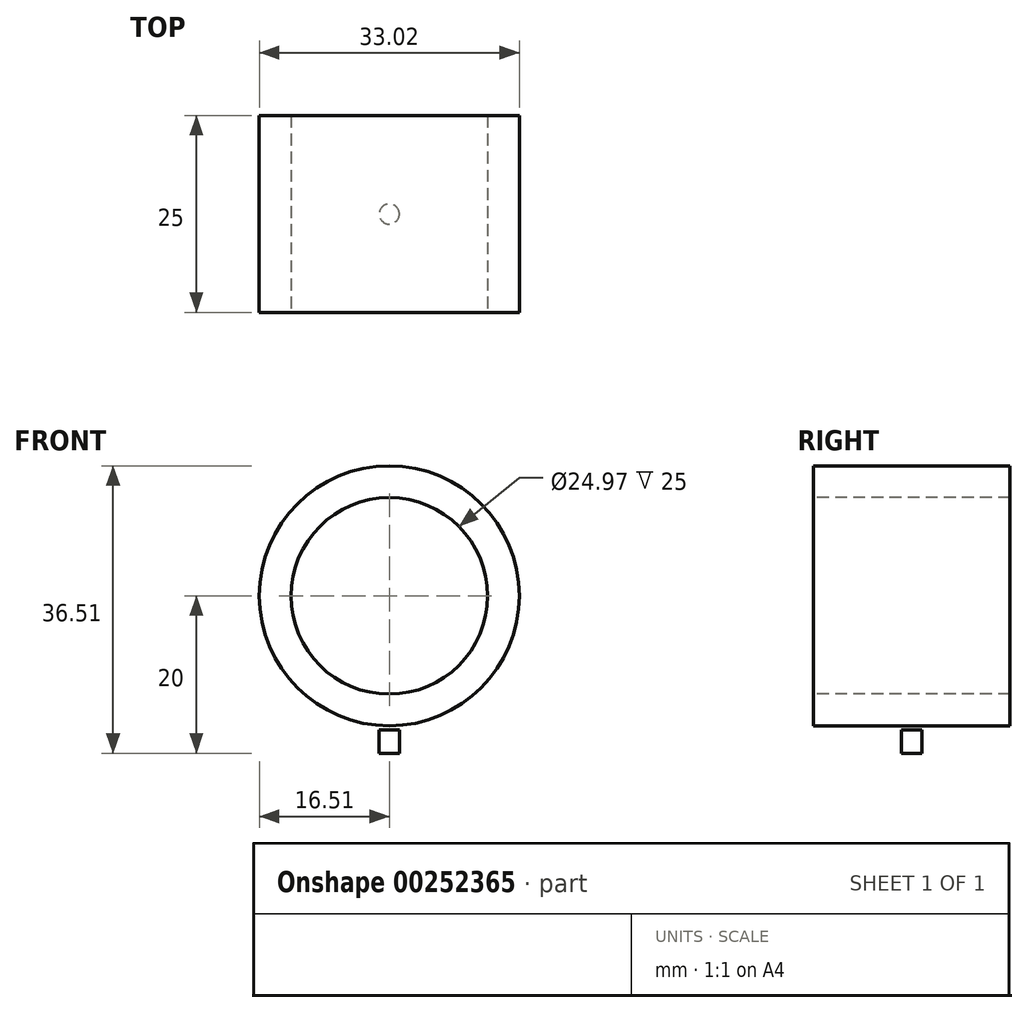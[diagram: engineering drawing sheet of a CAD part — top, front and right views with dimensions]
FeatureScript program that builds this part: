
annotation { "Feature Type Name" : "Feature", "Feature Type Description" : "" }
export const myFeature = defineFeature(function(context is Context, id is Id, definition is map)
    precondition{}
    {
        {
            var Q0;
            Q0=qCreatedBy(makeId("Front.planeOp"),FACE);
            var sketch = newSketch(context, id + "F0", { "sketchPlane" : qUnion([Q0])});
            skCircle(sketch, "E0", {"center": v(0, 0) * mm, "radius": 16.51 * mm});
            skLineSegment(sketch, "E1.bottom", {"start": v(3.39, -18.5) * mm, "end": v(-3.39, -18.5) * mm});
            skLineSegment(sketch, "E1.top", {"start": v(3.39, -14.53) * mm, "end": v(-3.39, -14.53) * mm});
            skLineSegment(sketch, "E1.left", {"start": v(3.39, -18.5) * mm, "end": v(3.39, -14.53) * mm});
            skLineSegment(sketch, "E1.right", {"start": v(-3.39, -18.5) * mm, "end": v(-3.39, -14.53) * mm});
            skPoint(sketch, "E1.middle", {"position": v(0, -16.51) * mm});
            skSolve(sketch);
        }
        {
            var Q0;
            Q0=makeQuery(id+"F0.imprint","IMPRINT",FACE,{"disambiguationData":[TD([[makeQuery(id+"F0.imprint","IMPRINT",EDGE,{"derivedFrom":sQuery(id+"F0.wireOp",EDGE,"E0")}),1.0]])]});
            extrude(context, id + "F1", {"entities" : qUnion([Q0]), "depth" : 25 * mm});
        }
        {
            var Q0;
            Q0=makeQuery(id+"F1.opExtrude","CAP_FACE",FACE,{"disambiguationData":[OSD([sQuery(id+"F0.wireOp",EDGE,"E0")])],"isStart":false});
            var sketch = newSketch(context, id + "F2", { "sketchPlane" : qUnion([Q0])});
            skCircle(sketch, "E2", {"center": v(0, 0) * mm, "radius": 12.48 * mm});
            skSolve(sketch);
        }
        {
            var Q0;
            Q0=makeQuery(id+"F2.imprint","IMPRINT",FACE,{"disambiguationData":[TD([[makeQuery(id+"F2.imprint","IMPRINT",EDGE,{"derivedFrom":sQuery(id+"F2.wireOp",EDGE,"E2")}),1.0]])]});
            extrude(context, id + "F3", {"entities" : qUnion([Q0]), "operationType" : NewBodyOperationType.REMOVE, "oppositeDirection" : true, "depth" : 30 * mm});
        }
        {
            var Q0;
            Q0=sQuery(id+"F0.wireOp",EDGE,"E1.top");
            var Q1;
            Q1=sQuery(id+"F0.wireOp",EDGE,"E1.bottom");
            var Q2;
            Q2=sQuery(id+"F0.wireOp",EDGE,"E1.right");
            var Q3;
            Q3=sQuery(id+"F0.wireOp",EDGE,"E1.left");
            extrude(context, id + "F4", {"bodyType" : ToolBodyType.SURFACE, "surfaceEntities" : qUnion([Q0, Q1, Q2, Q3]), "depth" : 25 * mm});
        }
        {
            var Q0;
            Q0=makeQuery(id+"F4.opExtrude","SWEPT_FACE",FACE,{"disambiguationData":[OSD([sQuery(id+"F0.wireOp",EDGE,"E1.bottom")])]});
            var sketch = newSketch(context, id + "F5", { "sketchPlane" : qUnion([Q0])});
            skCircle(sketch, "E3", {"center": v(0, -12.5) * mm, "radius": 1.29 * mm});
            skPoint(sketch, "E3.centerSnap0", {"position": v(3.39, -12.5) * mm});
            skSolve(sketch);
        }
        {
            var Q0;
            Q0=makeQuery(id+"F5.imprint","IMPRINT",FACE,{"disambiguationData":[TD([[makeQuery(id+"F5.imprint","IMPRINT",EDGE,{"derivedFrom":sQuery(id+"F5.wireOp",EDGE,"E3")}),1.0]])]});
            extrude(context, id + "F6", {"entities" : qUnion([Q0]), "endBound" : BoundingType.SYMMETRIC, "depth" : 3 * mm});
        }
    });
